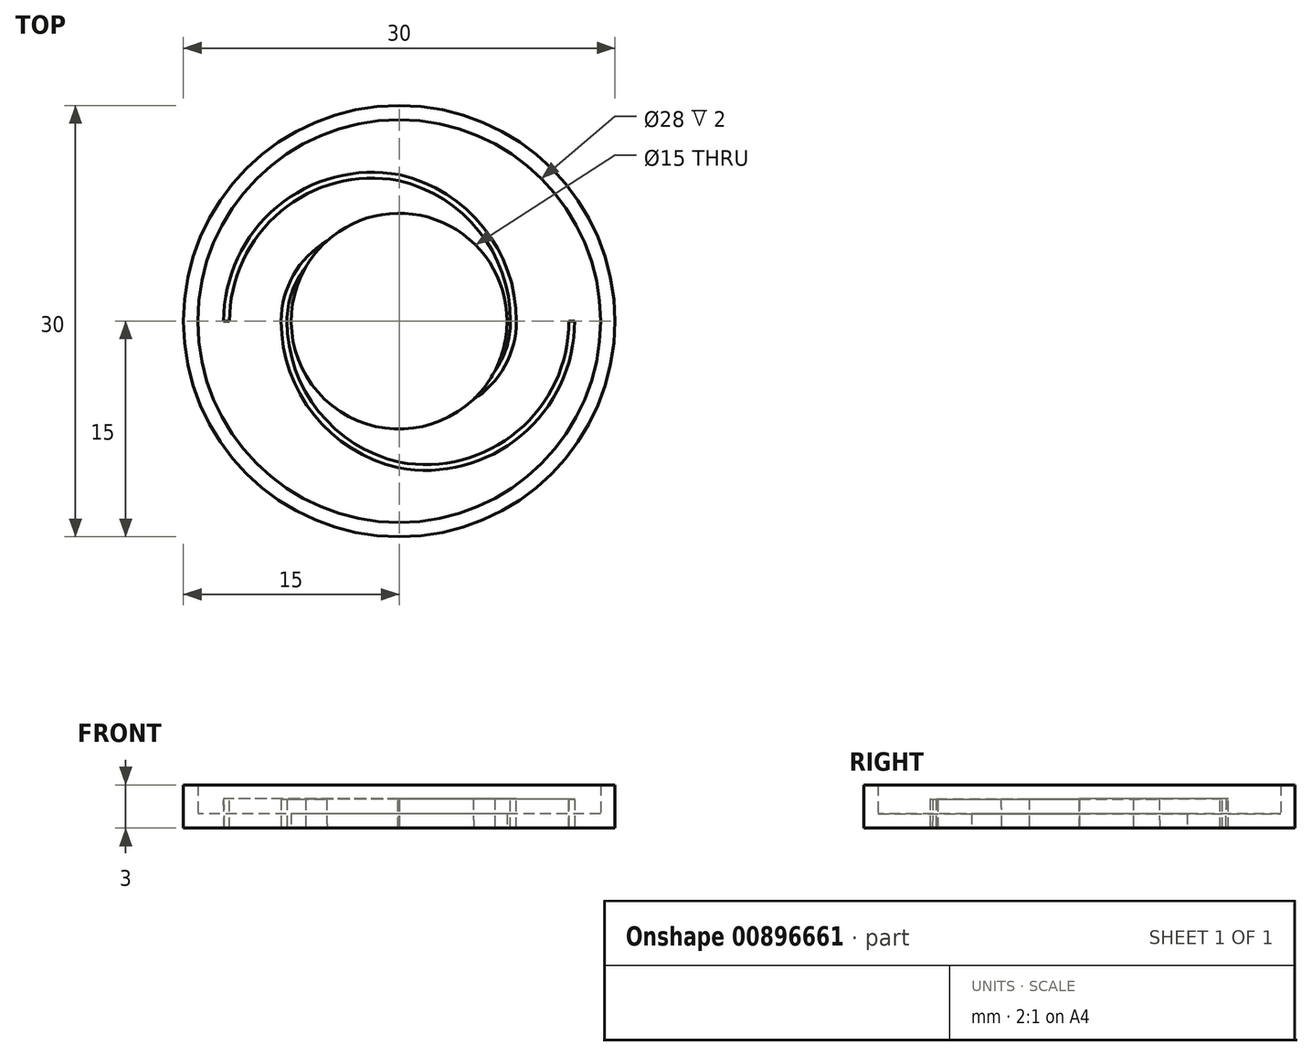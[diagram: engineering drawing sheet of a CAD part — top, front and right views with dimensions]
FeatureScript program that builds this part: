
annotation { "Feature Type Name" : "Feature", "Feature Type Description" : "" }
export const myFeature = defineFeature(function(context is Context, id is Id, definition is map)
    precondition{}
    {
        {
            var Q0;
            Q0=qCreatedBy(makeId("Top.planeOp"),FACE);
            var sketch = newSketch(context, id + "F0", { "sketchPlane" : qUnion([Q0])});
            skCircle(sketch, "E0", {"center": v(0, 0) * mm, "radius": 4.1 * mm});
            skSolve(sketch);
        }
        {
            var Q0;
            Q0=qCreatedBy(makeId("Top.planeOp"),FACE);
            var sketch = newSketch(context, id + "F1", { "sketchPlane" : qUnion([Q0])});
            skArc(sketch, "E1", {"start": v(4.1, 0) * mm, "mid": v(2.98, 3.64) * mm, "end": v(0, 6.02) * mm});
            skArc(sketch, "E2", {"start": v(0, 6.02) * mm, "mid": v(-5.5, 5) * mm, "end": v(-7.99, 0) * mm});
            skArc(sketch, "E3", {"start": v(-7.99, 0) * mm, "mid": v(-5.75, -6.4) * mm, "end": v(0, -10) * mm});
            skArc(sketch, "E4", {"start": v(0, -10) * mm, "mid": v(8.34, -7.81) * mm, "end": v(12, 0) * mm});
            skArc(sketch, "E5", {"start": v(12, 0) * mm, "mid": v(11.87, 2.1) * mm, "end": v(11.62, 4.2) * mm});
            skSolve(sketch);
        }
        {
            var Q0;
            Q0=qCreatedBy(makeId("Top.planeOp"),FACE);
            var sketch = newSketch(context, id + "F2", { "sketchPlane" : qUnion([Q0])});
            skArc(sketch, "E6", {"start": v(-4.13, 0) * mm, "mid": v(-3, -3.65) * mm, "end": v(-0.02, -6.02) * mm});
            skArc(sketch, "E7", {"start": v(-0.02, -6.02) * mm, "mid": v(5.48, -5) * mm, "end": v(7.97, 0) * mm});
            skArc(sketch, "E8", {"start": v(7.97, 0) * mm, "mid": v(5.73, 6.4) * mm, "end": v(-0.02, 10) * mm});
            skArc(sketch, "E9", {"start": v(-0.02, 10) * mm, "mid": v(-8.36, 7.81) * mm, "end": v(-12.01, 0) * mm});
            skSolve(sketch);
        }
        {
            var Q0;
            Q0=qCreatedBy(makeId("Top.planeOp"),FACE);
            var sketch = newSketch(context, id + "F3", { "sketchPlane" : qUnion([Q0])});
            skCircle(sketch, "E10", {"center": v(0, 0) * mm, "radius": 15 * mm});
            skSolve(sketch);
        }
        {
            var Q0;
            Q0 = qSketchRegion(id + "F3", true);
            extrude(context, id + "F4", {"entities" : qUnion([Q0]), "depth" : 3 * mm, "offsetDistance" : 25 * mm});
        }
        {
            var Q0;
            Q0=makeQuery(id+"F4.opExtrude","CAP_FACE",FACE,{"disambiguationData":[OSD([sQuery(id+"F3.wireOp",EDGE,"E10")])],"isStart":false});
            shell(context, id + "F5", {"entities" : qUnion([Q0]), "thickness" : 1 * mm});
        }
        {
            var Q0;
            Q0 = qSketchRegion(id + "F0", true);
            extrude(context, id + "F6", {"entities" : qUnion([Q0]), "depth" : 2 * mm, "offsetDistance" : 25 * mm});
        }
        {
            var Q0;
            Q0=makeQuery(id+"F6.opExtrude","CAP_FACE",FACE,{"disambiguationData":[OSD([sQuery(id+"F0.wireOp",EDGE,"E0")])],"isStart":false});
            shell(context, id + "F7", {"entities" : qUnion([Q0]), "thickness" : 0.6 * mm});
        }
        {
            var Q0;
            Q0 = qSketchRegion(id + "F2", true);
            var Q1;
            Q1 = qConstructionFilter(qBodyType(qCreatedBy(id + "F2" ,EDGE), BodyType.WIRE), ConstructionObject.NO);
            extrude(context, id + "F8", {"entities" : qUnion([Q0]), "bodyType" : ToolBodyType.SURFACE, "surfaceEntities" : qUnion([Q1]), "depth" : 5 * mm, "offsetDistance" : 25 * mm});
        }
        {
            var Q0;
            Q0 = qSketchRegion(id + "F1", true);
            var Q1;
            Q1 = qConstructionFilter(qBodyType(qCreatedBy(id + "F1" ,EDGE), BodyType.WIRE), ConstructionObject.NO);
            extrude(context, id + "F9", {"entities" : qUnion([Q0]), "bodyType" : ToolBodyType.SURFACE, "surfaceEntities" : qUnion([Q1]), "depth" : 5 * mm, "offsetDistance" : 25 * mm});
        }
        {
            var Q0;
            Q0=qCreatedBy(makeId("Front.planeOp"),FACE);
            var sketch = newSketch(context, id + "F10", { "sketchPlane" : qUnion([Q0])});
            skLineSegment(sketch, "E11", {"start": v(-12.19, 0) * mm, "end": v(-11.79, 0) * mm});
            skLineSegment(sketch, "E12", {"start": v(-11.79, 0) * mm, "end": v(-11.79, 2.03) * mm});
            skLineSegment(sketch, "E13", {"start": v(-11.79, 2.03) * mm, "end": v(-12.2, 2.03) * mm});
            skLineSegment(sketch, "E14", {"start": v(-12.2, 2.03) * mm, "end": v(-12.19, 0) * mm});
            skSolve(sketch);
        }
        {
            var Q0;
            Q0 = qSketchRegion(id + "F10", true);
            var Q1;
            Q1 = qConstructionFilter(qBodyType(qCreatedBy(id + "F2" ,EDGE), BodyType.WIRE), ConstructionObject.NO);
            sweep(context, id + "F11", {"profiles" : qUnion([Q0]), "path" : qUnion([Q1])});
        }
        {
            var Q0;
            Q0=qCreatedBy(makeId("Front.planeOp"),FACE);
            var sketch = newSketch(context, id + "F12", { "sketchPlane" : qUnion([Q0])});
            skLineSegment(sketch, "E15", {"start": v(12.2, 0) * mm, "end": v(11.8, 0) * mm});
            skLineSegment(sketch, "E16", {"start": v(11.8, 0) * mm, "end": v(11.8, 2) * mm});
            skLineSegment(sketch, "E17", {"start": v(11.8, 2) * mm, "end": v(12.2, 2) * mm});
            skLineSegment(sketch, "E18", {"start": v(12.2, 2) * mm, "end": v(12.2, 0) * mm});
            skSolve(sketch);
        }
        {
            var Q0;
            Q0 = qSketchRegion(id + "F12", true);
            var Q1;
            Q1=makeQuery(id+"F9.opExtrude","CAP_EDGE",EDGE,{"disambiguationData":[OSD([sQuery(id+"F1.wireOp",EDGE,"E4")])],"isStart":true});
            var Q2;
            Q2=makeQuery(id+"F9.opExtrude","CAP_EDGE",EDGE,{"disambiguationData":[OSD([sQuery(id+"F1.wireOp",EDGE,"E3")])],"isStart":true});
            var Q3;
            Q3=makeQuery(id+"F9.opExtrude","CAP_EDGE",EDGE,{"disambiguationData":[OSD([sQuery(id+"F1.wireOp",EDGE,"E2")])],"isStart":true});
            var Q4;
            Q4=makeQuery(id+"F9.opExtrude","CAP_EDGE",EDGE,{"disambiguationData":[OSD([sQuery(id+"F1.wireOp",EDGE,"E1")])],"isStart":true});
            sweep(context, id + "F13", {"profiles" : qUnion([Q0]), "path" : qUnion([Q1, Q2, Q3, Q4])});
        }
        {
            var Q0;
            Q0=makeQuery(id+"F0.imprint","IMPRINT",FACE,{"disambiguationData":[TD([[makeQuery(id+"F0.imprint","IMPRINT",EDGE,{"derivedFrom":sQuery(id+"F0.wireOp",EDGE,"E0")}),1.0]])]});
            var Q1;
            Q1=sQuery(id+"F0.wireOp",EDGE,"E0");
            extrude(context, id + "F14", {"entities" : qUnion([Q0]), "surfaceEntities" : qUnion([Q1]), "depth" : 2 * mm, "offsetDistance" : 25 * mm});
        }
        {
            var Q0;
            Q0=qCreatedBy(makeId("Top.planeOp"),FACE);
            var sketch = newSketch(context, id + "F15", { "sketchPlane" : qUnion([Q0])});
            skCircle(sketch, "E19", {"center": v(0, 0) * mm, "radius": 3.61 * mm});
            skSolve(sketch);
        }
        {
            var Q0;
            Q0 = qSketchRegion(id + "F15", true);
            extrude(context, id + "F16", {"entities" : qUnion([Q0]), "operationType" : NewBodyOperationType.REMOVE, "depth" : 6.4 * mm, "offsetDistance" : 25 * mm});
        }
        {
            var Q0;
            Q0 = qSketchRegion(id + "F0", true);
            extrude(context, id + "F17", {"entities" : qUnion([Q0]), "operationType" : NewBodyOperationType.REMOVE, "depth" : 25 * mm, "offsetDistance" : 25 * mm});
        }
        {
            var Q0;
            Q0=qCreatedBy(makeId("Top.planeOp"),FACE);
            var sketch = newSketch(context, id + "F18", { "sketchPlane" : qUnion([Q0])});
            skCircle(sketch, "E20", {"center": v(0, 0) * mm, "radius": 7.5 * mm});
            skSolve(sketch);
        }
        {
            var Q0;
            Q0 = qSketchRegion(id + "F18", true);
            extrude(context, id + "F19", {"entities" : qUnion([Q0]), "operationType" : NewBodyOperationType.REMOVE, "depth" : 25 * mm, "offsetDistance" : 25 * mm});
        }
    });
